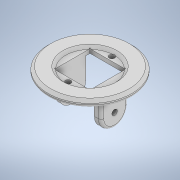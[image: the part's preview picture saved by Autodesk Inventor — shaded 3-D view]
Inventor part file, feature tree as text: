
AUTODESK INVENTOR PART (.ipt)
format: ipt  version: 2022 (Build 260153000, 153)  size: 210,944 bytes
history: native  units: in
note: dims shown in document units (in); Inventor stores cm internally (conversion verified against a paired STEP export)
features: extrude x6, sketch x6, chamfer x2, fillet x2
ambient origin geometry x8: Origin, YZ Plane, XZ Plane, XY Plane, X Axis, Y Axis, Z Axis, Center Point
bodies: Solid1 (feature_tree)
feature tree (16):
  extrude  "Extrusion1"  Depth=0.1969in TaperAngle=0.0deg
  extrude  "Extrusion2"  Depth=0.0787in TaperAngle=0.0deg
  chamfer  "Chamfer1"  Distance=0.0787in Angle=45.0deg
  extrude  "Extrusion3"  Depth=1.0394in
  extrude  "Extrusion4"  Depth=0.1575in
  extrude  "Extrusion5"  Depth=0.7874in TaperAngle=0.0deg
  fillet  "Fillet1"  Radius=0.1969in
  fillet  "Fillet2"  Radius=0.7874in
  extrude  "Extrusion6"  Depth=0.7874in
  chamfer  "Chamfer2"  Distance=1.0079in
  sketch  "Sketch1"  dims[d0=2.4409in d1=0.1969in d2=0.0in]
  sketch  "Sketch2"  dims[d3=1.5748in d4=0.0787in d5=0.0in d6=0.0787in d7=0.0787in d8=45.0deg]
  sketch  "Sketch3"  dims[d9=1.0394in d10=1.0394in]
  sketch  "Sketch4"  dims[d11=0.2362in d12=0.0in d13=0.1575in]
  sketch  "Sketch5"  dims[d14=0.1575in d15=0.2362in d16=0.0in d17=0.1969in d18=0.7874in]
  sketch  "Sketch6"  dims[d19=0.1969in d20=0.7874in d21=1.0079in d22=0.0in d23=0.3937in d24=0.0787in d25=0.1575in d26=1.9685in d27=0.0in d28=0.0787in d29=0.0787in d30=45.0deg d31=0.6142in d32=0.0344in d33=0.0197in d34=0.0344in]
